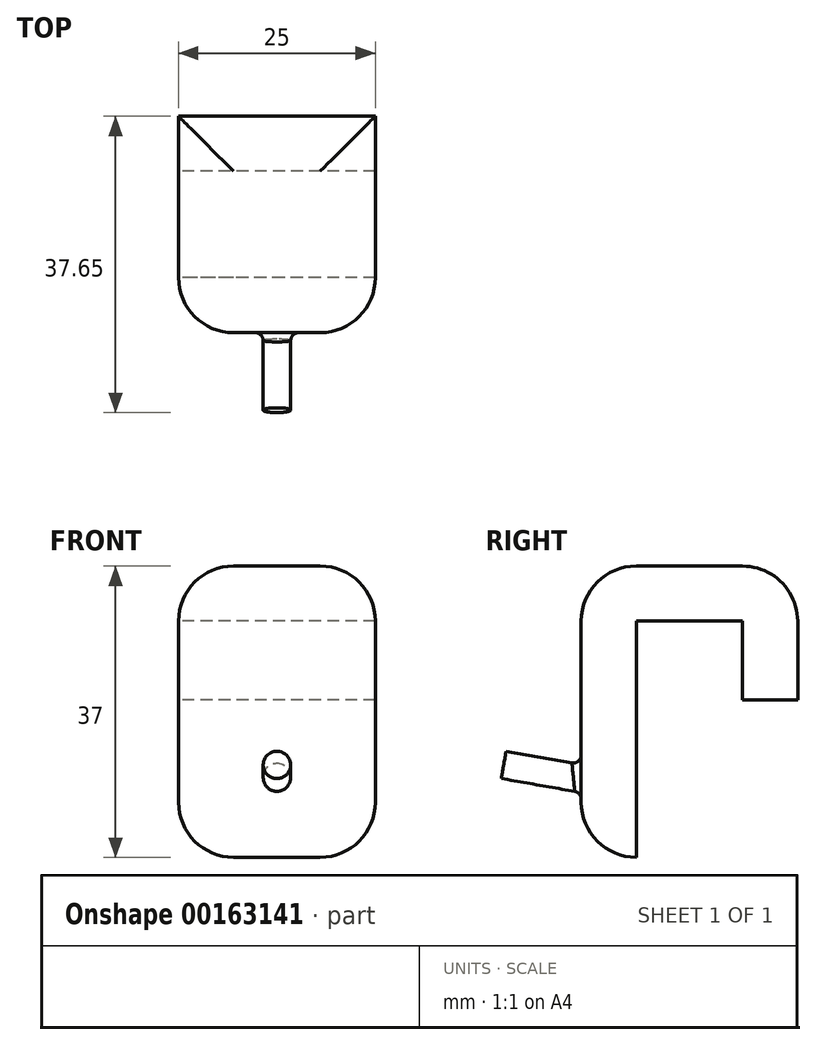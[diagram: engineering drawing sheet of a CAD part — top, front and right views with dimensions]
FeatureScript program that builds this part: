
annotation { "Feature Type Name" : "Feature", "Feature Type Description" : "" }
export const myFeature = defineFeature(function(context is Context, id is Id, definition is map)
    precondition{}
    {
        {
            var Q0;
            Q0=qCreatedBy(makeId("Right.planeOp"),FACE);
            var sketch = newSketch(context, id + "F0", { "sketchPlane" : qUnion([Q0])});
            skLineSegment(sketch, "E0", {"start": v(0, -15.82) * mm, "end": v(0, 21.18) * mm});
            skLineSegment(sketch, "E1", {"start": v(0, 21.18) * mm, "end": v(27.5, 21.18) * mm});
            skLineSegment(sketch, "E2", {"start": v(27.5, 21.18) * mm, "end": v(27.5, 4.18) * mm});
            skLineSegment(sketch, "E3", {"start": v(27.5, 4.18) * mm, "end": v(20.5, 4.18) * mm});
            skLineSegment(sketch, "E4", {"start": v(20.5, 4.18) * mm, "end": v(20.5, 14.18) * mm});
            skLineSegment(sketch, "E5", {"start": v(20.5, 14.18) * mm, "end": v(7, 14.18) * mm});
            skLineSegment(sketch, "E6", {"start": v(7, 14.18) * mm, "end": v(7, -15.82) * mm});
            skLineSegment(sketch, "E7", {"start": v(7, -15.82) * mm, "end": v(0, -15.82) * mm});
            skSolve(sketch);
        }
        {
            var Q0;
            Q0=makeQuery(id+"F0.imprint","IMPRINT",FACE,{"disambiguationData":[TD([[makeQuery(id+"F0.imprint","IMPRINT",EDGE,{"derivedFrom":sQuery(id+"F0.wireOp",EDGE,"E0")}),-1.0]])]});
            extrude(context, id + "F1", {"entities" : qUnion([Q0]), "depth" : 25 * mm});
        }
        {
            var Q0;
            Q0=makeQuery(id+"F1.opExtrude","SWEPT_FACE",FACE,{"disambiguationData":[OSD([sQuery(id+"F0.wireOp",EDGE,"E0")])]});
            var sketch = newSketch(context, id + "F2", { "sketchPlane" : qUnion([Q0])});
            skLineSegment(sketch, "E8", {"start": v(0, -5.82) * mm, "end": v(25, -5.82) * mm, "construction": true});
            skSolve(sketch);
        }
        {
            var Q0;
            Q0=sQuery(id+"F2.wireOp",EDGE,"E8");
            var Q1;
            Q1=makeQuery(id+"F1.opExtrude","CAP_EDGE",EDGE,{"disambiguationData":[OSD([sQuery(id+"F0.wireOp",EDGE,"E0")])],"isStart":false});
            cPlane(context, id + "F3", {"entities" : qUnion([Q0, Q1]), "cplaneType" : CPlaneType.LINE_ANGLE, "offset" : 25 * mm, "angle" : 350 * degree, "width" : 150 * mm, "height" : 150 * mm});
        }
        {
            var Q0;
            Q0=qCreatedBy(id+"F3.planeOp",FACE);
            var sketch = newSketch(context, id + "F4", { "sketchPlane" : qUnion([Q0])});
            skLineSegment(sketch, "E9.0", {"start": v(0, -5.73) * mm, "end": v(25, -5.73) * mm});
            skPoint(sketch, "E10", {"position": v(12.5, -5.73) * mm});
            skSolve(sketch);
        }
        {
            var Q0;
            Q0=makeQuery(id+"F1.opExtrude","CAP_EDGE",EDGE,{"disambiguationData":[OSD([sQuery(id+"F0.wireOp",EDGE,"E0")])],"isStart":false});
            var Q1;
            Q1=makeQuery(id+"F1.opExtrude","SWEPT_EDGE",EDGE,{"disambiguationData":[OSD([sQuery(id+"F0.wireOp",EDGE,"E0"),sQuery(id+"F0.wireOp",EDGE,"E1")])]});
            var Q2;
            Q2=makeQuery(id+"F1.opExtrude","CAP_EDGE",EDGE,{"disambiguationData":[OSD([sQuery(id+"F0.wireOp",EDGE,"E0")])],"isStart":true});
            var Q3;
            Q3=makeQuery(id+"F1.opExtrude","SWEPT_EDGE",EDGE,{"disambiguationData":[OSD([sQuery(id+"F0.wireOp",EDGE,"E0"),sQuery(id+"F0.wireOp",EDGE,"E7")])]});
            var Q4;
            Q4=makeQuery(id+"F1.opExtrude","CAP_EDGE",EDGE,{"disambiguationData":[OSD([sQuery(id+"F0.wireOp",EDGE,"E1")])],"isStart":false});
            var Q5;
            Q5=makeQuery(id+"F1.opExtrude","CAP_EDGE",EDGE,{"disambiguationData":[OSD([sQuery(id+"F0.wireOp",EDGE,"E1")])],"isStart":true});
            var Q6;
            Q6=makeQuery(id+"F1.opExtrude","CAP_EDGE",EDGE,{"disambiguationData":[OSD([sQuery(id+"F0.wireOp",EDGE,"E7")])],"isStart":false});
            var Q7;
            Q7=makeQuery(id+"F1.opExtrude","CAP_EDGE",EDGE,{"disambiguationData":[OSD([sQuery(id+"F0.wireOp",EDGE,"E7")])],"isStart":true});
            var Q8;
            Q8=makeQuery(id+"F1.opExtrude","SWEPT_EDGE",EDGE,{"disambiguationData":[OSD([sQuery(id+"F0.wireOp",EDGE,"E1"),sQuery(id+"F0.wireOp",EDGE,"E2")])]});
            fillet(context, id + "F5", {"entities" : qUnion([Q0, Q1, Q2, Q3, Q4, Q5, Q6, Q7, Q8]), "radius" : 7 * mm, "tangentPropagation" : true, "allowEdgeOverflow" : false});
        }
        {
            var Q0;
            Q0=qCreatedBy(id+"F3.planeOp",FACE);
            var sketch = newSketch(context, id + "F6", { "sketchPlane" : qUnion([Q0])});
            skPoint(sketch, "E11.0", {"position": v(12.5, -5.73) * mm});
            skCircle(sketch, "E12", {"center": v(12.5, -5.73) * mm, "radius": 1.75 * mm});
            skSolve(sketch);
        }
        {
            var Q0;
            Q0=makeQuery(id+"F6.imprint","IMPRINT",FACE,{"disambiguationData":[TD([[makeQuery(id+"F6.imprint","IMPRINT",EDGE,{"derivedFrom":sQuery(id+"F6.wireOp",EDGE,"E12")}),1.0]])]});
            extrude(context, id + "F7", {"entities" : qUnion([Q0]), "operationType" : NewBodyOperationType.ADD, "depth" : 10 * mm, "hasSecondDirection" : true, "secondDirectionOppositeDirection" : true, "secondDirectionDepth" : 5 * mm});
        }
        {
            var Q0;
            Q0=makeQuery(id+"F7.boolean.opBoolean","INTERSECT",EDGE,{"derivedFrom":[makeQuery(id+"F1.opExtrude","SWEPT_FACE",FACE,{"disambiguationData":[OSD([sQuery(id+"F0.wireOp",EDGE,"E0")])]}),makeQuery(id+"F7.opExtrude","SWEPT_FACE",FACE,{"disambiguationData":[OSD([sQuery(id+"F6.wireOp",EDGE,"E12")])]})]});
            fillet(context, id + "F8", {"entities" : qUnion([Q0]), "radius" : 1 * mm, "tangentPropagation" : true, "allowEdgeOverflow" : false});
        }
    });
